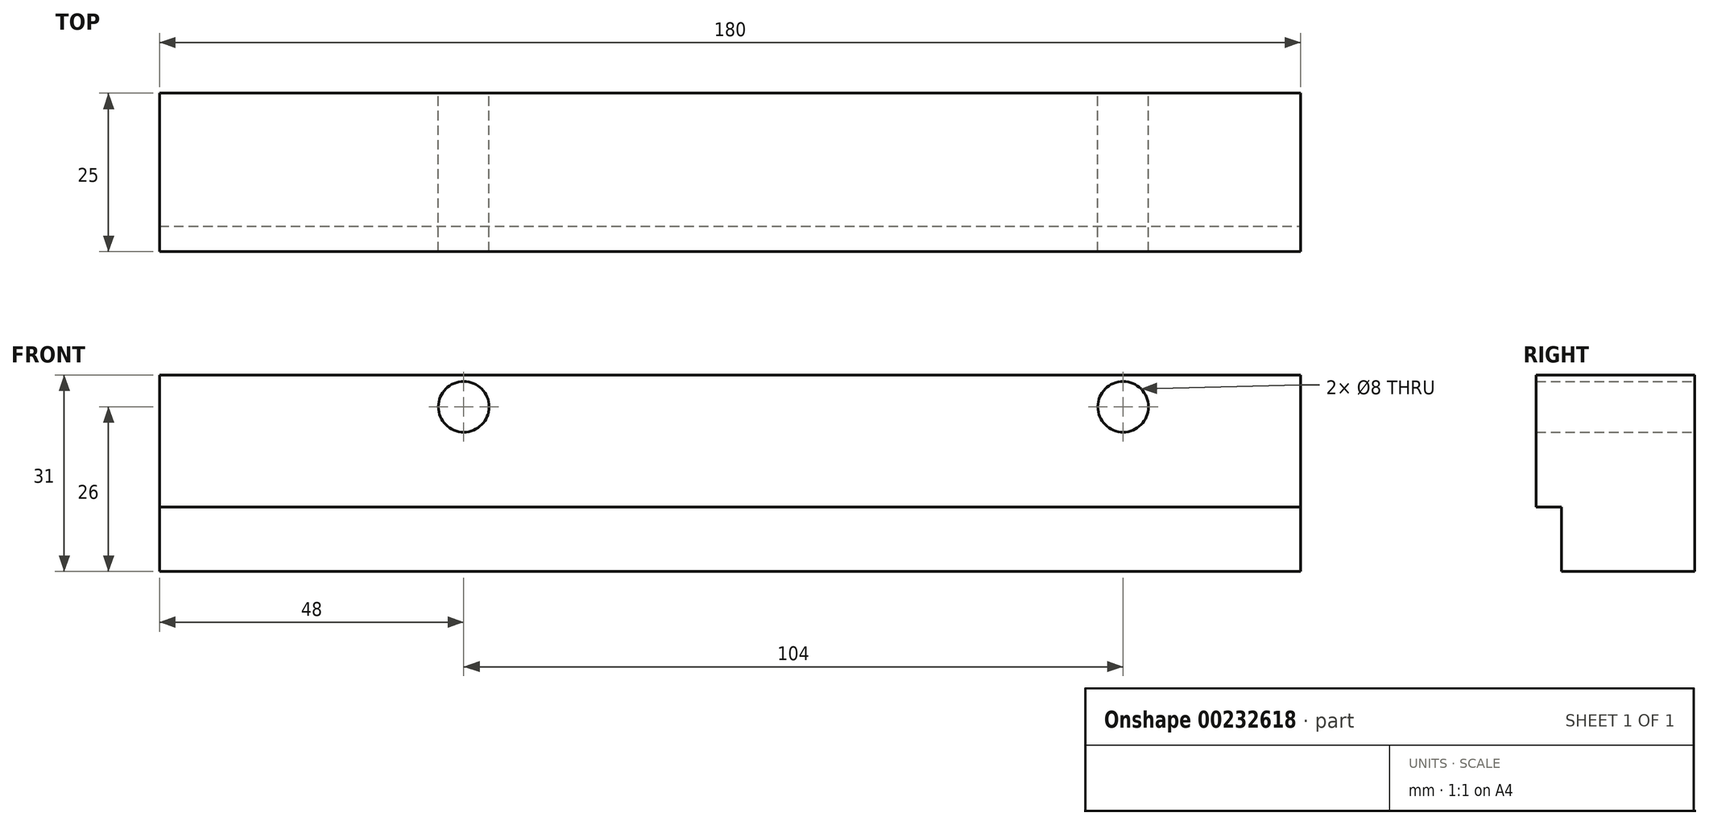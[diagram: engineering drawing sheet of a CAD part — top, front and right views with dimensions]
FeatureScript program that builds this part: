
annotation { "Feature Type Name" : "Feature", "Feature Type Description" : "" }
export const myFeature = defineFeature(function(context is Context, id is Id, definition is map)
    precondition{}
    {
        {
            var Q0;
            Q0=qCreatedBy(makeId("Front.planeOp"),FACE);
            var sketch = newSketch(context, id + "F0", { "sketchPlane" : qUnion([Q0])});
            skLineSegment(sketch, "E0.bottom", {"start": v(0, 0) * mm, "end": v(180, 0) * mm});
            skLineSegment(sketch, "E0.top", {"start": v(0, 31) * mm, "end": v(180, 31) * mm});
            skLineSegment(sketch, "E0.left", {"start": v(0, 0) * mm, "end": v(0, 31) * mm});
            skLineSegment(sketch, "E0.right", {"start": v(180, 0) * mm, "end": v(180, 31) * mm});
            skSolve(sketch);
        }
        {
            var Q0;
            Q0 = qSketchRegion(id + "F0", true);
            extrude(context, id + "F1", {"entities" : qUnion([Q0]), "depth" : 25 * mm});
        }
        {
            var Q0;
            Q0=makeQuery(id+"F1.opExtrude","CAP_FACE",FACE,{"disambiguationData":[OSD([sQuery(id+"F0.wireOp",EDGE,"E0.bottom"),sQuery(id+"F0.wireOp",EDGE,"E0.top"),sQuery(id+"F0.wireOp",EDGE,"E0.left"),sQuery(id+"F0.wireOp",EDGE,"E0.right")])],"isStart":true});
            var sketch = newSketch(context, id + "F2", { "sketchPlane" : qUnion([Q0])});
            skCircle(sketch, "E1", {"center": v(-152, 26) * mm, "radius": 4 * mm});
            skCircle(sketch, "E2", {"center": v(-48, 26) * mm, "radius": 4 * mm});
            skSolve(sketch);
        }
        {
            var Q0;
            Q0 = qSketchRegion(id + "F2", true);
            extrude(context, id + "F3", {"entities" : qUnion([Q0]), "operationType" : NewBodyOperationType.REMOVE, "endBound" : BoundingType.THROUGH_ALL, "oppositeDirection" : true, "depth" : 25 * mm});
        }
        {
            var Q0;
            Q0=makeQuery(id+"F1.opExtrude","SWEPT_FACE",FACE,{"disambiguationData":[OSD([sQuery(id+"F0.wireOp",EDGE,"E0.right")])]});
            var sketch = newSketch(context, id + "F4", { "sketchPlane" : qUnion([Q0])});
            skLineSegment(sketch, "E3.bottom", {"start": v(-25, 0) * mm, "end": v(-21, 0) * mm});
            skLineSegment(sketch, "E3.top", {"start": v(-25, 10.2) * mm, "end": v(-21, 10.2) * mm});
            skLineSegment(sketch, "E3.left", {"start": v(-25, 0) * mm, "end": v(-25, 10.2) * mm});
            skLineSegment(sketch, "E3.right", {"start": v(-21, 0) * mm, "end": v(-21, 10.2) * mm});
            skSolve(sketch);
        }
        {
            var Q0;
            Q0 = qSketchRegion(id + "F4", true);
            extrude(context, id + "F5", {"entities" : qUnion([Q0]), "operationType" : NewBodyOperationType.REMOVE, "endBound" : BoundingType.THROUGH_ALL, "oppositeDirection" : true, "depth" : 25 * mm});
        }
    });
